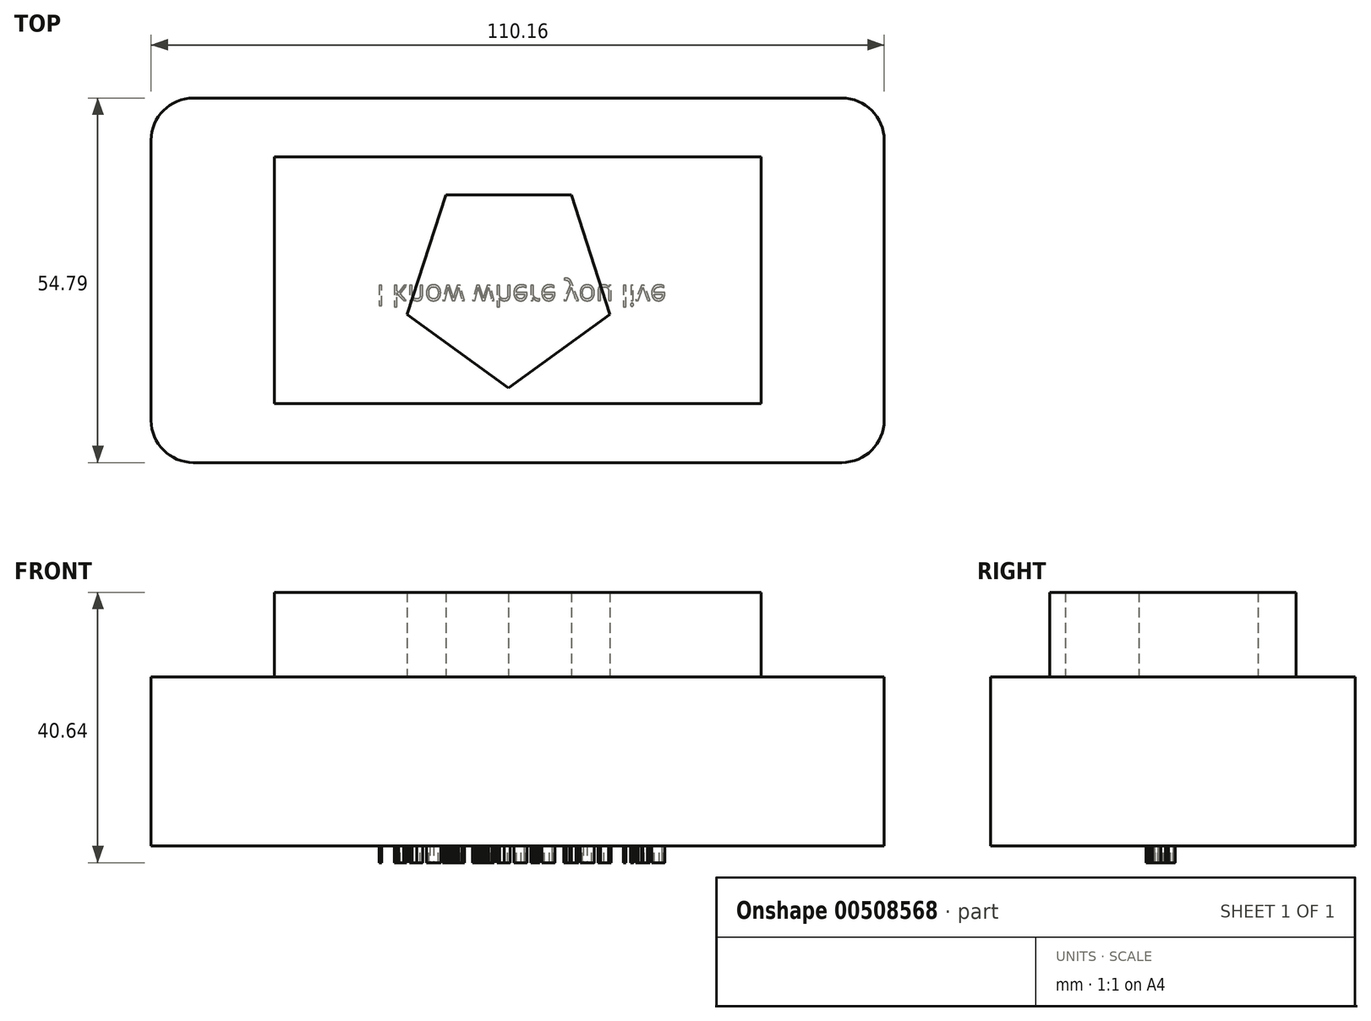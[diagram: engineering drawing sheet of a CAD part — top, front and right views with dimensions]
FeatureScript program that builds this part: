
annotation { "Feature Type Name" : "Feature", "Feature Type Description" : "" }
export const myFeature = defineFeature(function(context is Context, id is Id, definition is map)
    precondition{}
    {
        {
            var Q0;
            Q0=qCreatedBy(makeId("Top.planeOp"),FACE);
            var sketch = newSketch(context, id + "F0", { "sketchPlane" : qUnion([Q0])});
            skLineSegment(sketch, "E0.bottom", {"start": v(-47.35, 31.24) * mm, "end": v(50.11, 31.24) * mm});
            skLineSegment(sketch, "E0.top", {"start": v(-47.35, -23.55) * mm, "end": v(50.11, -23.55) * mm});
            skLineSegment(sketch, "E0.left", {"start": v(-53.7, 24.89) * mm, "end": v(-53.7, -17.2) * mm});
            skLineSegment(sketch, "E0.right", {"start": v(56.46, 24.89) * mm, "end": v(56.46, -17.2) * mm});
            skPoint(sketch, "E1.visualSharp", {"position": v(-53.7, 31.24) * mm});
            skArc(sketch, "E1.filletArc", {"start": v(-47.35, 31.24) * mm, "mid": v(-51.84, 29.38) * mm, "end": v(-53.7, 24.89) * mm});
            skPoint(sketch, "E2.visualSharp", {"position": v(-53.7, -23.55) * mm});
            skArc(sketch, "E2.filletArc", {"start": v(-53.7, -17.2) * mm, "mid": v(-51.84, -21.69) * mm, "end": v(-47.35, -23.55) * mm});
            skPoint(sketch, "E3.visualSharp", {"position": v(56.46, -23.55) * mm});
            skArc(sketch, "E3.filletArc", {"start": v(50.11, -23.55) * mm, "mid": v(54.6, -21.69) * mm, "end": v(56.46, -17.2) * mm});
            skPoint(sketch, "E4.visualSharp", {"position": v(56.46, 31.24) * mm});
            skArc(sketch, "E4.filletArc", {"start": v(56.46, 24.89) * mm, "mid": v(54.6, 29.38) * mm, "end": v(50.11, 31.24) * mm});
            skSolve(sketch);
        }
        {
            var Q0;
            Q0=makeQuery(id+"F0.imprint","IMPRINT",FACE,{"disambiguationData":[TD([[makeQuery(id+"F0.imprint","IMPRINT",EDGE,{"derivedFrom":sQuery(id+"F0.wireOp",EDGE,"E0.bottom")}),-1.0]])]});
            extrude(context, id + "F1", {"entities" : qUnion([Q0]), "oppositeDirection" : true, "depth" : 25.4 * mm, "offsetDistance" : 25.4 * mm});
        }
        {
            var Q0;
            Q0=qCreatedBy(makeId("Right.planeOp"),FACE);
            var sketch = newSketch(context, id + "F2", { "sketchPlane" : qUnion([Q0])});
            skLineSegment(sketch, "E5.bottom", {"start": v(27.69, 0) * mm, "end": v(23.75, 0) * mm});
            skLineSegment(sketch, "E5.top", {"start": v(27.69, 55.87) * mm, "end": v(23.75, 55.87) * mm});
            skLineSegment(sketch, "E5.left", {"start": v(27.69, 0) * mm, "end": v(27.69, 55.87) * mm});
            skLineSegment(sketch, "E5.right", {"start": v(23.75, 0) * mm, "end": v(23.75, 55.87) * mm});
            skLineSegment(sketch, "E6.bottom", {"start": v(-14.1, 0) * mm, "end": v(-18.23, 0) * mm});
            skLineSegment(sketch, "E6.top", {"start": v(-14.1, 55.87) * mm, "end": v(-18.23, 55.87) * mm});
            skLineSegment(sketch, "E6.left", {"start": v(-14.1, 0) * mm, "end": v(-14.1, 55.87) * mm});
            skLineSegment(sketch, "E6.right", {"start": v(-18.23, 0) * mm, "end": v(-18.23, 55.87) * mm});
            skSolve(sketch);
        }
        {
            var Q0;
            Q0=makeQuery(id+"F2.imprint","IMPRINT",FACE,{"disambiguationData":[TD([[makeQuery(id+"F2.imprint","IMPRINT",EDGE,{"derivedFrom":sQuery(id+"F2.wireOp",EDGE,"E6.bottom")}),-1.0]])]});
            var Q1;
            Q1=makeQuery(id+"F2.imprint","IMPRINT",FACE,{"disambiguationData":[TD([[makeQuery(id+"F2.imprint","IMPRINT",EDGE,{"derivedFrom":sQuery(id+"F2.wireOp",EDGE,"E5.bottom")}),-1.0]])]});
            extrude(context, id + "F3", {"entities" : qUnion([Q0, Q1]), "operationType" : NewBodyOperationType.REMOVE, "oppositeDirection" : true, "depth" : 6.35 * mm, "offsetDistance" : 25.4 * mm});
        }
        {
            var Q0;
            Q0=qCreatedBy(makeId("Top.planeOp"),FACE);
            var sketch = newSketch(context, id + "F4", { "sketchPlane" : qUnion([Q0])});
            skLineSegment(sketch, "E7.bottom", {"start": v(-35.18, -14.68) * mm, "end": v(37.94, -14.68) * mm});
            skLineSegment(sketch, "E7.top", {"start": v(-35.18, 22.37) * mm, "end": v(37.94, 22.37) * mm});
            skLineSegment(sketch, "E7.left", {"start": v(-35.18, -14.68) * mm, "end": v(-35.18, 22.37) * mm});
            skLineSegment(sketch, "E7.right", {"start": v(37.94, -14.68) * mm, "end": v(37.94, 22.37) * mm});
            skCircle(sketch, "E8.cCircle", {"center": v(0, 3.69) * mm, "radius": 12.98 * mm, "construction": true});
            skLineSegment(sketch, "E8.0", {"start": v(-9.43, 16.66) * mm, "end": v(9.43, 16.66) * mm});
            skLineSegment(sketch, "E8.1", {"start": v(9.43, 16.66) * mm, "end": v(15.25, -1.27) * mm});
            skLineSegment(sketch, "E8.2", {"start": v(15.25, -1.27) * mm, "end": v(0, -12.35) * mm});
            skLineSegment(sketch, "E8.3", {"start": v(0, -12.35) * mm, "end": v(-15.25, -1.27) * mm});
            skLineSegment(sketch, "E8.4", {"start": v(-15.25, -1.27) * mm, "end": v(-9.43, 16.66) * mm});
            skPoint(sketch, "E8.0.midPoint", {"position": v(0, 16.66) * mm});
            skSolve(sketch);
        }
        {
            var Q0;
            Q0 = qSketchRegion(id + "F4", true);
            var Q1;
            Q1=makeQuery(id+"F1.opExtrude","CAP_FACE",FACE,{"disambiguationData":[OSD([sQuery(id+"F0.wireOp",EDGE,"E0.bottom"),sQuery(id+"F0.wireOp",EDGE,"E0.top"),sQuery(id+"F0.wireOp",EDGE,"E0.left"),sQuery(id+"F0.wireOp",EDGE,"E0.right"),sQuery(id+"F0.wireOp",EDGE,"E1.filletArc"),sQuery(id+"F0.wireOp",EDGE,"E2.filletArc"),sQuery(id+"F0.wireOp",EDGE,"E3.filletArc"),sQuery(id+"F0.wireOp",EDGE,"E4.filletArc")])],"isStart":false});
            var Q2;
            Q2 = qSketchRegion(id + "F6", true);
            extrude(context, id + "F5", {"entities" : qUnion([Q0, Q1, Q2]), "operationType" : NewBodyOperationType.ADD, "depth" : 12.7 * mm, "offsetDistance" : 25.4 * mm});
        }
        {
            var Q0;
            Q0=makeQuery(id+"F1.opExtrude","CAP_FACE",FACE,{"disambiguationData":[OSD([sQuery(id+"F0.wireOp",EDGE,"E0.bottom"),sQuery(id+"F0.wireOp",EDGE,"E0.top"),sQuery(id+"F0.wireOp",EDGE,"E0.left"),sQuery(id+"F0.wireOp",EDGE,"E0.right"),sQuery(id+"F0.wireOp",EDGE,"E1.filletArc"),sQuery(id+"F0.wireOp",EDGE,"E2.filletArc"),sQuery(id+"F0.wireOp",EDGE,"E3.filletArc"),sQuery(id+"F0.wireOp",EDGE,"E4.filletArc")])],"isStart":false});
            var sketch = newSketch(context, id + "F6", { "sketchPlane" : qUnion([Q0])});
            skText(sketch, "E9", { "text": "I know where you live", "fontName": "OpenSans-Regular.ttf"});
            const initialGuessF6  = {"E9": [-0.01984, -0.00312, 1, 0, 0.00312]};
            skSetInitialGuess(sketch, initialGuessF6);
            skSolve(sketch);
        }
        {
            var Q0;
            Q0 = qSketchRegion(id + "F6", true);
            extrude(context, id + "F7", {"entities" : qUnion([Q0]), "operationType" : NewBodyOperationType.ADD, "depth" : 2.54 * mm, "offsetDistance" : 25.4 * mm});
        }
    });
